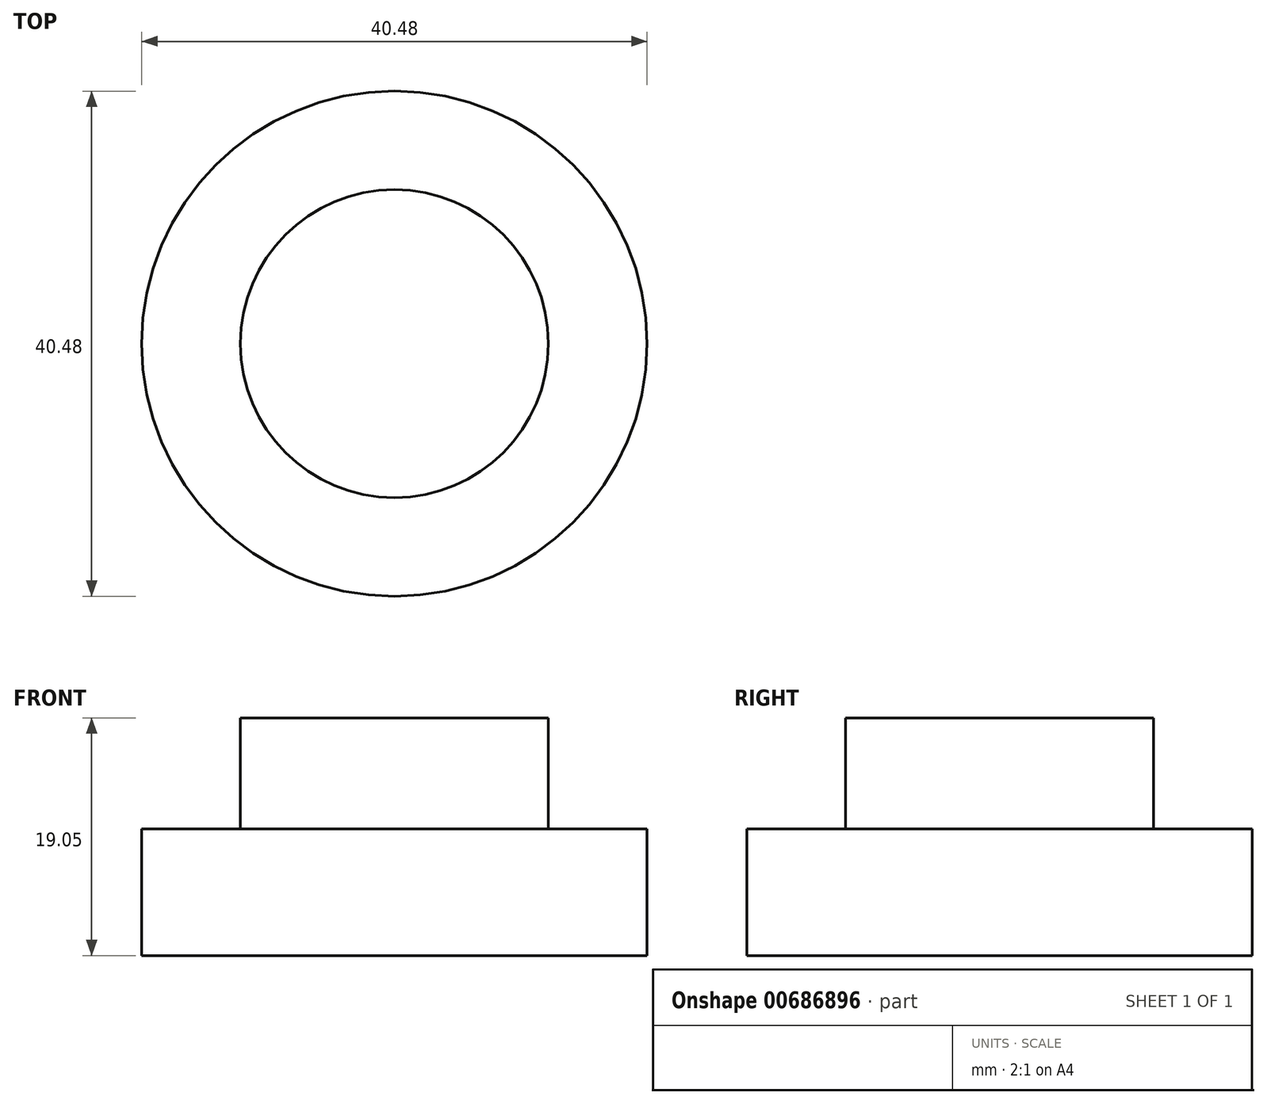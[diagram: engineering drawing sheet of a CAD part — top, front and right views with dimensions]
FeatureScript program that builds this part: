
annotation { "Feature Type Name" : "Feature", "Feature Type Description" : "" }
export const myFeature = defineFeature(function(context is Context, id is Id, definition is map)
    precondition{}
    {
        {
            var Q0;
            Q0=qCreatedBy(makeId("Top.planeOp"),FACE);
            var sketch = newSketch(context, id + "F0", { "sketchPlane" : qUnion([Q0])});
            skCircle(sketch, "E0", {"center": v(0, 0) * mm, "radius": 20.24 * mm});
            skSolve(sketch);
        }
        {
            var Q0;
            Q0=makeQuery(id+"F0.imprint","IMPRINT",FACE,{"disambiguationData":[TD([[makeQuery(id+"F0.imprint","IMPRINT",EDGE,{"derivedFrom":sQuery(id+"F0.wireOp",EDGE,"E0")}),1.0]])]});
            extrude(context, id + "F1", {"entities" : qUnion([Q0]), "depth" : 10.16 * mm, "offsetDistance" : 25.4 * mm});
        }
        {
            var Q0;
            Q0=makeQuery(id+"F1.opExtrude","CAP_FACE",FACE,{"disambiguationData":[OSD([sQuery(id+"F0.wireOp",EDGE,"E0")])],"isStart":false});
            var sketch = newSketch(context, id + "F2", { "sketchPlane" : qUnion([Q0])});
            skCircle(sketch, "E1", {"center": v(0, 0) * mm, "radius": 12.34 * mm});
            skSolve(sketch);
        }
        {
            var Q0;
            Q0=makeQuery(id+"F2.imprint","IMPRINT",FACE,{"disambiguationData":[TD([[makeQuery(id+"F2.imprint","IMPRINT",EDGE,{"derivedFrom":sQuery(id+"F2.wireOp",EDGE,"E1")}),1.0]])]});
            extrude(context, id + "F3", {"entities" : qUnion([Q0]), "operationType" : NewBodyOperationType.ADD, "depth" : 8.9 * mm, "offsetDistance" : 25.4 * mm});
        }
        {
            var Q0;
            Q0=qCreatedBy(makeId("Front.planeOp"),FACE);
            var sketch = newSketch(context, id + "F4", { "sketchPlane" : qUnion([Q0])});
            skFitSpline(sketch, "E2", {"points": [v(-12.11, 18.93) * mm, v(-16.73, 183.49) * mm, v(-18.22, 214.3) * mm, v(-16.81, 214.58) * mm, v(-13.99, 217.26) * mm, v(-14.62, 225.2) * mm, v(-18.21, 229.02) * mm, v(-20.96, 229.02) * mm, v(-21.6, 230.7) * mm, v(-22.84, 248.83) * mm, v(-23.42, 258.92) * mm, v(-23.98, 275.83) * mm, v(-20.33, 273.74) * mm, v(-8.97, 268.6) * mm, v(6.35, 260.98) * mm, v(12.24, 255.8) * mm, v(17.15, 248.83) * mm, v(19.61, 242.44) * mm, v(21.28, 235.9) * mm, v(21.28, 227.71) * mm, v(17.38, 131.9) * mm, v(14.62, 70.07) * mm, v(12.17, 16.93) * mm, v(11.79, 13.35) * mm, v(8.4, 12.03) * mm, v(0, 12.78) * mm, v(-10.44, 13.35) * mm, v(-12.11, 18.93) * mm]});
            skSolve(sketch);
        }
        {
            var Q0;
            Q0=makeQuery(id+"F4.imprint","IMPRINT",FACE,{"disambiguationData":[TD([[makeQuery(id+"F4.imprint","IMPRINT",EDGE,{"derivedFrom":sQuery(id+"F4.wireOp",EDGE,"E2")}),-1.0]])]});
            extrude(context, id + "F5", {"entities" : qUnion([Q0]), "operationType" : NewBodyOperationType.ADD, "depth" : 0.25 * mm, "offsetDistance" : 25.4 * mm});
        }
        {
            var Q0;
            Q0=makeQuery(id+"F5.opExtrude","CAP_FACE",FACE,{"disambiguationData":[OSD([sQuery(id+"F4.wireOp",EDGE,"E2")])],"isStart":true});
            extrude(context, id + "F6", {"entities" : qUnion([Q0]), "operationType" : NewBodyOperationType.ADD, "depth" : 0.25 * mm, "offsetDistance" : 25.4 * mm});
        }
        {
            var Q0;
            Q0=makeQuery(id+"F6.opExtrude","CAP_FACE",FACE,{"disambiguationData":[OSD([sQuery(id+"F4.wireOp",EDGE,"E2")])],"isStart":false});
            extrude(context, id + "F7", {"entities" : qUnion([Q0]), "operationType" : NewBodyOperationType.ADD, "depth" : 2.3 * mm, "offsetDistance" : 25.4 * mm});
        }
        {
            var Q0;
            Q0=makeQuery(id+"F5.opExtrude","CAP_FACE",FACE,{"disambiguationData":[OSD([sQuery(id+"F4.wireOp",EDGE,"E2")])],"isStart":false});
            extrude(context, id + "F8", {"entities" : qUnion([Q0]), "operationType" : NewBodyOperationType.ADD, "depth" : 2.3 * mm, "offsetDistance" : 25.4 * mm});
        }
        {
            var Q0;
            Q0=qCreatedBy(makeId("Front.planeOp"),FACE);
            var sketch = newSketch(context, id + "F9", { "sketchPlane" : qUnion([Q0])});
            skLineSegment(sketch, "E3", {"start": v(5.87, 261.95) * mm, "end": v(-28.44, 277.08) * mm});
            skLineSegment(sketch, "E4", {"start": v(-28.44, 277.08) * mm, "end": v(-7.62, 282.54) * mm});
            skLineSegment(sketch, "E5", {"start": v(-7.62, 282.54) * mm, "end": v(5.87, 261.95) * mm});
            skSolve(sketch);
        }
        {
            var Q0;
            Q0=makeQuery(id+"F9.imprint","IMPRINT",FACE,{"disambiguationData":[TD([[makeQuery(id+"F9.imprint","IMPRINT",EDGE,{"derivedFrom":sQuery(id+"F9.wireOp",EDGE,"E3")}),-1.0]])]});
            extrude(context, id + "F10", {"entities" : qUnion([Q0]), "operationType" : NewBodyOperationType.ADD, "depth" : 25.4 * mm, "offsetDistance" : 25.4 * mm});
        }
        {
            var Q0;
            Q0=makeQuery(id+"F10.opExtrude","CAP_FACE",FACE,{"disambiguationData":[OSD([sQuery(id+"F9.wireOp",EDGE,"E3"),sQuery(id+"F9.wireOp",EDGE,"E4"),sQuery(id+"F9.wireOp",EDGE,"E5")])],"isStart":false});
            extrude(context, id + "F11", {"entities" : qUnion([Q0]), "operationType" : NewBodyOperationType.REMOVE, "oppositeDirection" : true, "depth" : 50.8 * mm, "offsetDistance" : 25.4 * mm});
        }
        {
            var Q0;
            Q0=makeQuery(id+"F8.opExtrude","CAP_FACE",FACE,{"disambiguationData":[OSD([sQuery(id+"F4.wireOp",EDGE,"E2")])],"isStart":false});
            extrude(context, id + "F12", {"entities" : qUnion([Q0]), "operationType" : NewBodyOperationType.REMOVE, "oppositeDirection" : true, "depth" : 1.27 * mm, "offsetDistance" : 25.4 * mm});
        }
        {
            var Q0;
            Q0=makeQuery(id+"F7.opExtrude","CAP_FACE",FACE,{"disambiguationData":[OSD([sQuery(id+"F4.wireOp",EDGE,"E2")])],"isStart":false});
            extrude(context, id + "F13", {"entities" : qUnion([Q0]), "operationType" : NewBodyOperationType.REMOVE, "oppositeDirection" : true, "depth" : 1.27 * mm, "offsetDistance" : 25.4 * mm});
        }
        {
            var Q0;
            Q0=makeQuery(id+"F12.boolean.opBoolean","COPY",FACE,{"derivedFrom":makeQuery(id+"F12.opExtrude","CAP_FACE",FACE,{"disambiguationData":[OSD([sQuery(id+"F4.wireOp",EDGE,"E2")])],"isStart":false})});
            extrude(context, id + "F14", {"entities" : qUnion([Q0]), "operationType" : NewBodyOperationType.REMOVE, "oppositeDirection" : true, "depth" : 25.4 * mm, "offsetDistance" : 25.4 * mm});
        }
    });
